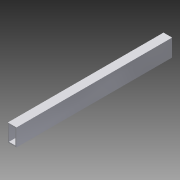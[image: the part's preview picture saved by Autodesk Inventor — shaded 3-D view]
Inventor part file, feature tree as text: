
AUTODESK INVENTOR PART (.ipt)
format: ipt  version: 2015 (Build 190159000, 159)  size: 80,384 bytes
history: native  units: in
note: dims shown in document units (in); Inventor stores cm internally (conversion verified against a paired STEP export)
features: extrude x1, sketch x1
ambient origin geometry x8: Origin, YZ Plane, XZ Plane, XY Plane, X Axis, Y Axis, Z Axis, Center Point
bodies: Solid1 (feature_tree)
feature tree (2):
  extrude  "Extrusion1"  Depth=18.0in TaperAngle=0.0deg
  sketch  "Sketch1"  dims[d0=1.0in d1=2.0in d2=0.125in d3=18.0in d4=0.0in]
